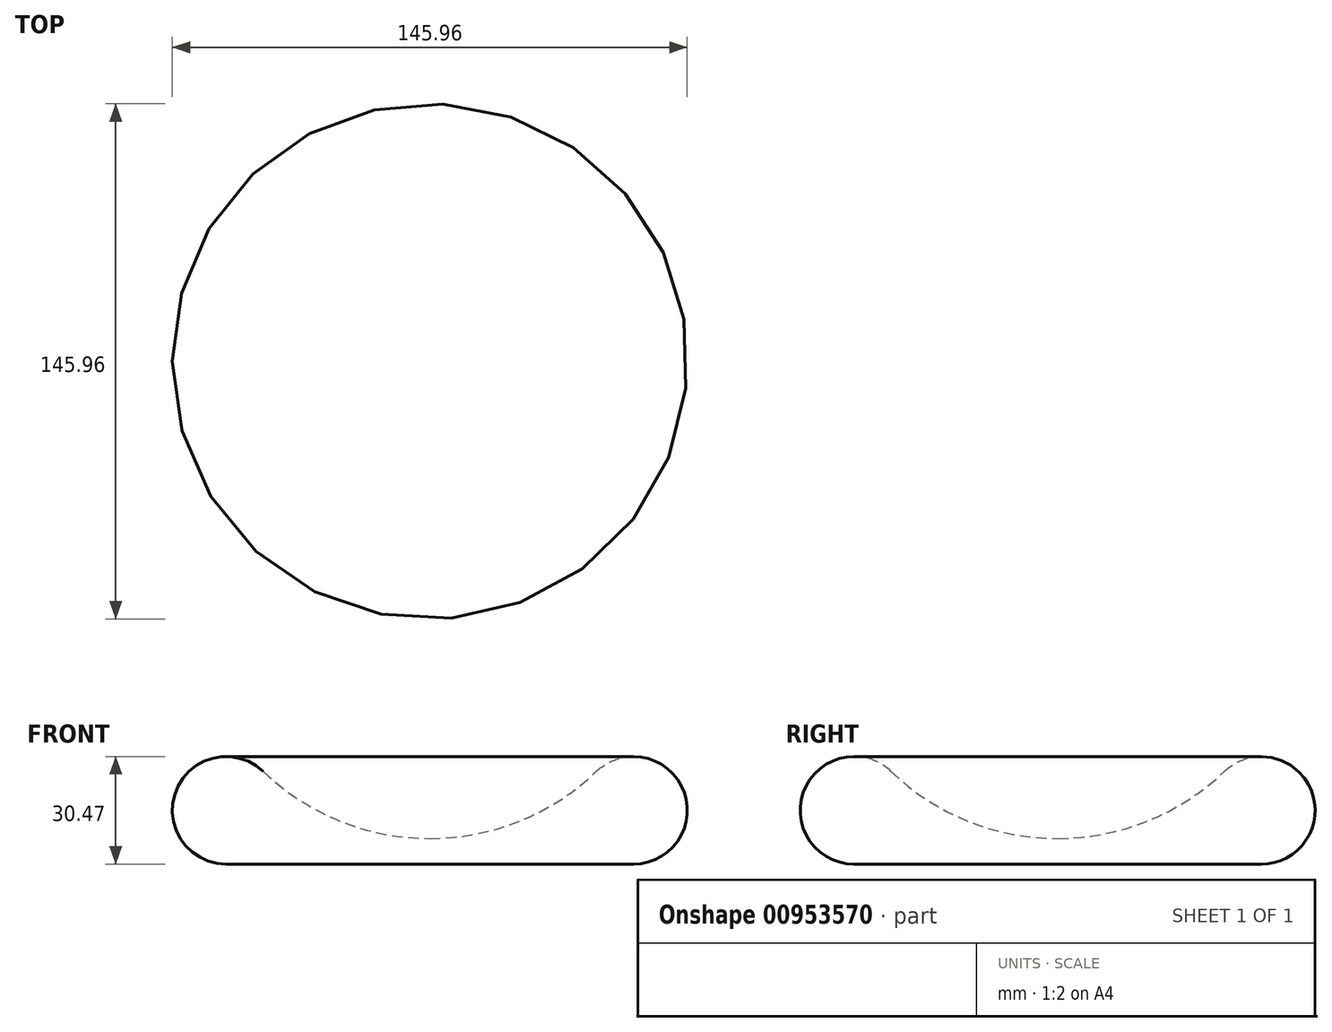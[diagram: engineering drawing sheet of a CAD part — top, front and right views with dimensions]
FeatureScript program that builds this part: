
annotation { "Feature Type Name" : "Feature", "Feature Type Description" : "" }
export const myFeature = defineFeature(function(context is Context, id is Id, definition is map)
    precondition{}
    {
        {
            var Q0;
            Q0=qCreatedBy(makeId("Front.planeOp"),FACE);
            var sketch = newSketch(context, id + "F0", { "sketchPlane" : qUnion([Q0])});
            skArc(sketch, "E0", {"start": v(-47.2, 26.23) * mm, "mid": v(-71.88, 20.92) * mm, "end": v(-57.74, 0) * mm});
            skArc(sketch, "E1", {"start": v(-47.2, 26.23) * mm, "mid": v(-25.43, 12.18) * mm, "end": v(0, 7.26) * mm});
            skLineSegment(sketch, "E2", {"start": v(0, 0) * mm, "end": v(0, 7.26) * mm});
            skLineSegment(sketch, "E3", {"start": v(0, 0) * mm, "end": v(-57.74, 0) * mm});
            skSolve(sketch);
        }
        {
            var Q0;
            Q0=makeQuery(id+"F0.imprint","IMPRINT",FACE,{"disambiguationData":[TD([[makeQuery(id+"F0.imprint","IMPRINT",EDGE,{"derivedFrom":sQuery(id+"F0.wireOp",EDGE,"E0")}),1.0]])]});
            var Q1;
            Q1=sQuery(id+"F0.wireOp",EDGE,"E2");
            revolve(context, id + "F1", {"surfaceOperationType" : NewSurfaceOperationType.NEW, "entities" : qUnion([Q0]), "axis" : qUnion([Q1]), "revolveType" : RevolveType.FULL});
        }
    });
